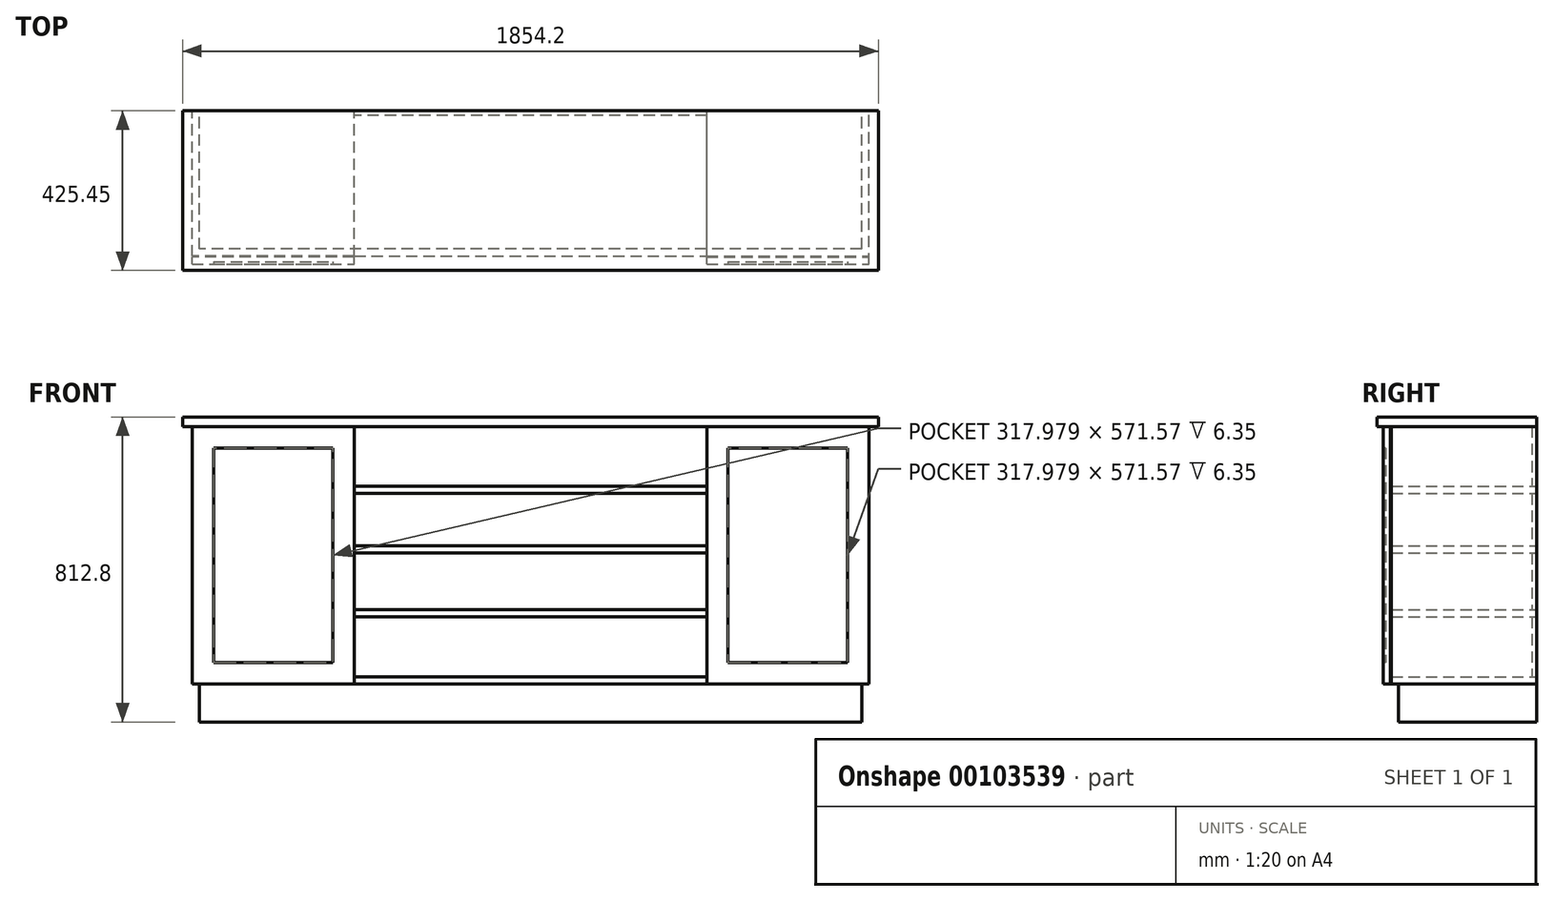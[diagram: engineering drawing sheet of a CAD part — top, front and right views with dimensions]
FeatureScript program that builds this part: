
annotation { "Feature Type Name" : "Feature", "Feature Type Description" : "" }
export const myFeature = defineFeature(function(context is Context, id is Id, definition is map)
    precondition{}
    {
        {
            var Q0;
            Q0=qCreatedBy(makeId("Front.planeOp"),FACE);
            var sketch = newSketch(context, id + "F0", { "sketchPlane" : qUnion([Q0])});
            skLineSegment(sketch, "E0.left", {"start": v(-901.7, 385.95) * mm, "end": v(-901.7, -299.85) * mm});
            skLineSegment(sketch, "E0.right", {"start": v(901.7, 385.95) * mm, "end": v(901.7, -299.85) * mm});
            skLineSegment(sketch, "E1", {"start": v(-901.7, 385.95) * mm, "end": v(-927.1, 385.95) * mm});
            skLineSegment(sketch, "E2", {"start": v(-927.1, 385.95) * mm, "end": v(-927.1, 411.35) * mm});
            skLineSegment(sketch, "E3", {"start": v(-927.1, 411.35) * mm, "end": v(927.1, 411.35) * mm});
            skLineSegment(sketch, "E4", {"start": v(927.1, 411.35) * mm, "end": v(927.1, 385.95) * mm});
            skLineSegment(sketch, "E5", {"start": v(901.7, 385.95) * mm, "end": v(927.1, 385.95) * mm});
            skLineSegment(sketch, "E6", {"start": v(-901.7, -299.85) * mm, "end": v(-882.65, -299.85) * mm});
            skLineSegment(sketch, "E7", {"start": v(-882.65, -299.85) * mm, "end": v(-882.65, -401.45) * mm});
            skLineSegment(sketch, "E8", {"start": v(-882.65, -401.45) * mm, "end": v(882.65, -401.45) * mm});
            skLineSegment(sketch, "E9", {"start": v(882.65, -401.45) * mm, "end": v(882.65, -299.85) * mm});
            skLineSegment(sketch, "E10", {"start": v(-469.5, 385.95) * mm, "end": v(-469.5, -299.85) * mm});
            skLineSegment(sketch, "E11", {"start": v(-901.7, 385.95) * mm, "end": v(-469.5, 385.95) * mm});
            skLineSegment(sketch, "E12", {"start": v(-469.5, -299.85) * mm, "end": v(-901.7, -299.85) * mm});
            skLineSegment(sketch, "E13", {"start": v(901.7, 385.95) * mm, "end": v(469.5, 385.95) * mm});
            skLineSegment(sketch, "E14", {"start": v(469.5, 385.95) * mm, "end": v(469.5, -299.85) * mm});
            skLineSegment(sketch, "E15", {"start": v(-469.5, -299.85) * mm, "end": v(469.5, -299.85) * mm});
            skLineSegment(sketch, "E16", {"start": v(469.5, -299.85) * mm, "end": v(901.7, -299.85) * mm});
            skLineSegment(sketch, "E17", {"start": v(469.5, 385.95) * mm, "end": v(-469.5, 385.95) * mm});
            skLineSegment(sketch, "E18.bottom", {"start": v(-844.59, 328.84) * mm, "end": v(-526.6, 328.84) * mm});
            skLineSegment(sketch, "E18.top", {"start": v(-844.59, -242.73) * mm, "end": v(-526.6, -242.73) * mm});
            skLineSegment(sketch, "E18.left", {"start": v(-844.59, 328.84) * mm, "end": v(-844.59, -242.73) * mm});
            skLineSegment(sketch, "E18.right", {"start": v(-526.6, 328.84) * mm, "end": v(-526.6, -242.73) * mm});
            skLineSegment(sketch, "E19.bottom", {"start": v(526.6, 328.84) * mm, "end": v(844.59, 328.84) * mm});
            skLineSegment(sketch, "E19.top", {"start": v(526.6, -242.73) * mm, "end": v(844.59, -242.73) * mm});
            skLineSegment(sketch, "E19.left", {"start": v(526.6, 328.84) * mm, "end": v(526.6, -242.73) * mm});
            skLineSegment(sketch, "E19.right", {"start": v(844.59, 328.84) * mm, "end": v(844.59, -242.73) * mm});
            skLineSegment(sketch, "E20", {"start": v(-526.6, 328.84) * mm, "end": v(-526.6, 385.95) * mm, "construction": true});
            skLineSegment(sketch, "E21", {"start": v(-526.6, 385.95) * mm, "end": v(-526.6, 328.84) * mm, "construction": true});
            skLineSegment(sketch, "E22", {"start": v(-526.6, 328.84) * mm, "end": v(-469.5, 328.84) * mm, "construction": true});
            skLineSegment(sketch, "E23", {"start": v(526.6, -242.73) * mm, "end": v(469.5, -242.73) * mm, "construction": true});
            skLineSegment(sketch, "E24", {"start": v(469.5, -242.73) * mm, "end": v(526.6, -242.73) * mm, "construction": true});
            skLineSegment(sketch, "E25", {"start": v(526.6, -242.73) * mm, "end": v(526.6, -299.85) * mm, "construction": true});
            skLineSegment(sketch, "E26", {"start": v(844.59, 328.84) * mm, "end": v(844.59, 385.95) * mm, "construction": true});
            skLineSegment(sketch, "E27", {"start": v(844.59, 385.95) * mm, "end": v(844.59, 328.84) * mm, "construction": true});
            skLineSegment(sketch, "E28", {"start": v(844.59, 328.84) * mm, "end": v(901.7, 328.84) * mm, "construction": true});
            skLineSegment(sketch, "E29", {"start": v(-844.59, -242.73) * mm, "end": v(-844.59, -299.85) * mm, "construction": true});
            skLineSegment(sketch, "E30", {"start": v(-469.5, -299.85) * mm, "end": v(-469.5, -280.8) * mm});
            skLineSegment(sketch, "E31", {"start": v(-469.5, -280.8) * mm, "end": v(469.5, -280.8) * mm});
            skLineSegment(sketch, "E32", {"start": v(469.5, -121.65) * mm, "end": v(-469.5, -121.65) * mm});
            skLineSegment(sketch, "E33", {"start": v(-469.5, -121.65) * mm, "end": v(-469.5, -102.6) * mm});
            skLineSegment(sketch, "E34", {"start": v(-469.5, -102.6) * mm, "end": v(469.5, -102.6) * mm});
            skLineSegment(sketch, "E35", {"start": v(469.5, 207.73) * mm, "end": v(-469.5, 207.73) * mm});
            skLineSegment(sketch, "E36", {"start": v(-469.5, 207.73) * mm, "end": v(-469.5, 226.78) * mm});
            skLineSegment(sketch, "E37", {"start": v(-469.5, 226.78) * mm, "end": v(469.5, 226.78) * mm});
            skLineSegment(sketch, "E38", {"start": v(-469.5, 67.6) * mm, "end": v(469.5, 67.6) * mm});
            skLineSegment(sketch, "E39", {"start": v(469.5, 48.56) * mm, "end": v(-469.5, 48.56) * mm});
            skPoint(sketch, "E40.endSnap0", {"position": v(0, 48.56) * mm});
            skPoint(sketch, "E41.endSnap0", {"position": v(0, 67.6) * mm});
            skLineSegment(sketch, "E42", {"start": v(-844.59, -242.73) * mm, "end": v(-901.7, -242.73) * mm, "construction": true});
            skLineSegment(sketch, "E43", {"start": v(299, 385.95) * mm, "end": v(299, 226.78) * mm, "construction": true});
            skLineSegment(sketch, "E44", {"start": v(299, 226.78) * mm, "end": v(299, 207.73) * mm, "construction": true});
            skLineSegment(sketch, "E45", {"start": v(299, 207.73) * mm, "end": v(299, 67.6) * mm, "construction": true});
            skLineSegment(sketch, "E46", {"start": v(299, 67.6) * mm, "end": v(299, 48.56) * mm, "construction": true});
            skLineSegment(sketch, "E47", {"start": v(299, 48.56) * mm, "end": v(299, -102.6) * mm, "construction": true});
            skLineSegment(sketch, "E48", {"start": v(299, -102.6) * mm, "end": v(299, -121.65) * mm, "construction": true});
            skLineSegment(sketch, "E49", {"start": v(299, -121.65) * mm, "end": v(299, -280.8) * mm, "construction": true});
            skLineSegment(sketch, "E50", {"start": v(299, -280.8) * mm, "end": v(299, -299.85) * mm, "construction": true});
            skSolve(sketch);
        }
        {
            var Q0;
            {var subQ5=sQuery(id+"F0.wireOp",EDGE,"E0.left");Q0=makeQuery(id+"F0.imprint","IMPRINT",FACE,{"disambiguationData":[TD([[makeQuery(id+"F0.imprint","IMPRINT",EDGE,{"derivedFrom":subQ5}),1.0]])]});}
            var Q1;
            {var subQ9=sQuery(id+"F0.wireOp",EDGE,"E0.right");Q1=makeQuery(id+"F0.imprint","IMPRINT",FACE,{"disambiguationData":[TD([[makeQuery(id+"F0.imprint","IMPRINT",EDGE,{"derivedFrom":subQ9}),-1.0]])]});}
            var Q2;
            Q2=makeQuery(id+"F0.imprint","IMPRINT",FACE,{"disambiguationData":[TD([[makeQuery(id+"F0.imprint","IMPRINT",EDGE,{"derivedFrom":sQuery(id+"F0.wireOp",EDGE,"E18.bottom")}),-1.0]])]});
            var Q3;
            Q3=makeQuery(id+"F0.imprint","IMPRINT",FACE,{"disambiguationData":[TD([[makeQuery(id+"F0.imprint","IMPRINT",EDGE,{"derivedFrom":sQuery(id+"F0.wireOp",EDGE,"E19.bottom")}),-1.0]])]});
            extrude(context, id + "F1", {"entities" : qUnion([Q0, Q1, Q2, Q3]), "depth" : 408.94 * mm});
        }
        {
            var Q0;
            {var subQ0=sQuery(id+"F0.wireOp",EDGE,"E35");Q0=makeQuery(id+"F0.imprint","IMPRINT",FACE,{"disambiguationData":[TD([[makeQuery(id+"F0.imprint","IMPRINT",EDGE,{"derivedFrom":subQ0}),-1.0]])]});}
            var Q1;
            {var subQ0=sQuery(id+"F0.wireOp",EDGE,"E38");Q1=makeQuery(id+"F0.imprint","IMPRINT",FACE,{"disambiguationData":[TD([[makeQuery(id+"F0.imprint","IMPRINT",EDGE,{"derivedFrom":subQ0}),-1.0]])]});}
            var Q2;
            {var subQ0=sQuery(id+"F0.wireOp",EDGE,"E32");Q2=makeQuery(id+"F0.imprint","IMPRINT",FACE,{"disambiguationData":[TD([[makeQuery(id+"F0.imprint","IMPRINT",EDGE,{"derivedFrom":subQ0}),-1.0]])]});}
            var Q3;
            {var subQ0=sQuery(id+"F0.wireOp",EDGE,"E15");Q3=makeQuery(id+"F0.imprint","IMPRINT",FACE,{"disambiguationData":[TD([[makeQuery(id+"F0.imprint","IMPRINT",EDGE,{"derivedFrom":subQ0}),1.0]])]});}
            extrude(context, id + "F2", {"entities" : qUnion([Q0, Q1, Q2, Q3]), "depth" : 387.35 * mm});
        }
        {
            var Q0;
            Q0=makeQuery(id+"F0.imprint","IMPRINT",FACE,{"disambiguationData":[TD([[makeQuery(id+"F0.imprint","IMPRINT",EDGE,{"derivedFrom":sQuery(id+"F0.wireOp",EDGE,"E1")}),-1.0]])]});
            extrude(context, id + "F3", {"entities" : qUnion([Q0]), "depth" : 425.45 * mm});
        }
        {
            var Q0;
            Q0=makeQuery(id+"F1.opExtrude","SWEPT_FACE",FACE,{"disambiguationData":[OSD([sQuery(id+"F0.wireOp",EDGE,"E0.left")])]});
            var sketch = newSketch(context, id + "F4", { "sketchPlane" : qUnion([Q0])});
            skLineSegment(sketch, "E51", {"start": v(408.94, 52.42) * mm, "end": v(389.9, 52.42) * mm, "construction": true});
            skLineSegment(sketch, "E52", {"start": v(389.9, -299.85) * mm, "end": v(389.9, 385.95) * mm});
            skLineSegment(sketch, "E53", {"start": v(389.9, 385.95) * mm, "end": v(387.35, 385.95) * mm});
            skLineSegment(sketch, "E54", {"start": v(387.35, 385.95) * mm, "end": v(387.35, -299.85) * mm});
            skLineSegment(sketch, "E55", {"start": v(387.35, -299.85) * mm, "end": v(389.9, -299.85) * mm});
            skLineSegment(sketch, "E56", {"start": v(389.9, 52.42) * mm, "end": v(387.35, 52.42) * mm, "construction": true});
            skPoint(sketch, "E56.endSnap0", {"position": v(387.35, 43.05) * mm});
            skSolve(sketch);
        }
        {
            var Q0;
            Q0=makeQuery(id+"F4.imprint","IMPRINT",FACE,{"disambiguationData":[TD([[makeQuery(id+"F4.imprint","IMPRINT",EDGE,{"derivedFrom":sQuery(id+"F4.wireOp",EDGE,"E52")}),1.0]])]});
            extrude(context, id + "F5", {"entities" : qUnion([Q0]), "operationType" : NewBodyOperationType.REMOVE, "endBound" : BoundingType.UP_TO_NEXT, "oppositeDirection" : true, "depth" : 25.4 * mm});
        }
        {
            var Q0;
            Q0=makeQuery(id+"F1.opExtrude","SWEPT_FACE",FACE,{"disambiguationData":[OSD([sQuery(id+"F0.wireOp",EDGE,"E0.right")])]});
            var sketch = newSketch(context, id + "F6", { "sketchPlane" : qUnion([Q0])});
            skLineSegment(sketch, "E57", {"start": v(-387.35, 385.95) * mm, "end": v(-387.35, -299.85) * mm});
            skPoint(sketch, "E58.endSnap0", {"position": v(-387.35, 43.05) * mm});
            skLineSegment(sketch, "E59.MirrorCS", {"start": v(-387.35, -299.85) * mm, "end": v(-389.9, -299.85) * mm});
            skLineSegment(sketch, "E60.MirrorCS", {"start": v(-389.9, 385.95) * mm, "end": v(-387.35, 385.95) * mm});
            skLineSegment(sketch, "E61.MirrorCS", {"start": v(-389.9, -299.85) * mm, "end": v(-389.9, 385.95) * mm});
            skLineSegment(sketch, "E62", {"start": v(-389.9, 43.05) * mm, "end": v(-408.94, 43.05) * mm, "construction": true});
            skSolve(sketch);
        }
        {
            var Q0;
            Q0=makeQuery(id+"F6.imprint","IMPRINT",FACE,{"disambiguationData":[TD([[makeQuery(id+"F6.imprint","IMPRINT",EDGE,{"derivedFrom":sQuery(id+"F6.wireOp",EDGE,"E57")}),-1.0]])]});
            extrude(context, id + "F7", {"entities" : qUnion([Q0]), "endBound" : BoundingType.UP_TO_NEXT, "oppositeDirection" : true, "depth" : 25.4 * mm});
        }
        {
            var Q0;
            {var subQ1=sQuery(id+"F0.wireOp",EDGE,"E7");Q0=makeQuery(id+"F0.imprint","IMPRINT",FACE,{"disambiguationData":[TD([[makeQuery(id+"F0.imprint","IMPRINT",EDGE,{"derivedFrom":subQ1}),1.0]])]});}
            extrude(context, id + "F8", {"entities" : qUnion([Q0]), "depth" : 368.3 * mm});
        }
        {
            var Q0;
            {var subQ0=sQuery(id+"F0.wireOp",EDGE,"E17");Q0=makeQuery(id+"F0.imprint","IMPRINT",FACE,{"disambiguationData":[TD([[makeQuery(id+"F0.imprint","IMPRINT",EDGE,{"derivedFrom":subQ0}),1.0]])]});}
            var Q1;
            {var subQ0=sQuery(id+"F0.wireOp",EDGE,"E35");Q1=makeQuery(id+"F0.imprint","IMPRINT",FACE,{"disambiguationData":[TD([[makeQuery(id+"F0.imprint","IMPRINT",EDGE,{"derivedFrom":subQ0}),1.0]])]});}
            var Q2;
            {var subQ0=sQuery(id+"F0.wireOp",EDGE,"E34");Q2=makeQuery(id+"F0.imprint","IMPRINT",FACE,{"disambiguationData":[TD([[makeQuery(id+"F0.imprint","IMPRINT",EDGE,{"derivedFrom":subQ0}),1.0]])]});}
            var Q3;
            {var subQ0=sQuery(id+"F0.wireOp",EDGE,"E31");Q3=makeQuery(id+"F0.imprint","IMPRINT",FACE,{"disambiguationData":[TD([[makeQuery(id+"F0.imprint","IMPRINT",EDGE,{"derivedFrom":subQ0}),1.0]])]});}
            extrude(context, id + "F9", {"entities" : qUnion([Q0, Q1, Q2, Q3]), "depth" : 12.7 * mm});
        }
        {
            var Q0;
            Q0=makeQuery(id+"F1.opExtrude","CAP_FACE",FACE,{"disambiguationData":[OSD([sQuery(id+"F0.wireOp",EDGE,"E0.left"),sQuery(id+"F0.wireOp",EDGE,"E10"),sQuery(id+"F0.wireOp",EDGE,"E11"),sQuery(id+"F0.wireOp",EDGE,"E12"),sQuery(id+"F0.wireOp",EDGE,"E30"),sQuery(id+"F0.wireOp",EDGE,"E33"),sQuery(id+"F0.wireOp",EDGE,"E36")])],"isStart":false});
            var sketch = newSketch(context, id + "F10", { "sketchPlane" : qUnion([Q0])});
            skLineSegment(sketch, "E63.0", {"start": v(-844.59, 328.84) * mm, "end": v(-526.6, 328.84) * mm});
            skLineSegment(sketch, "E64.0", {"start": v(-526.6, 328.84) * mm, "end": v(-526.6, -242.73) * mm});
            skLineSegment(sketch, "E65.0", {"start": v(-844.59, -242.73) * mm, "end": v(-526.6, -242.73) * mm});
            skLineSegment(sketch, "E66.0", {"start": v(-844.59, 328.84) * mm, "end": v(-844.59, -242.73) * mm});
            skLineSegment(sketch, "E67.0", {"start": v(526.6, 328.84) * mm, "end": v(526.6, -242.73) * mm});
            skLineSegment(sketch, "E68.0", {"start": v(526.6, 328.84) * mm, "end": v(844.59, 328.84) * mm});
            skLineSegment(sketch, "E69.0", {"start": v(844.59, 328.84) * mm, "end": v(844.59, -242.73) * mm});
            skLineSegment(sketch, "E70.0", {"start": v(526.6, -242.73) * mm, "end": v(844.59, -242.73) * mm});
            skSolve(sketch);
        }
        {
            var Q0;
            Q0=makeQuery(id+"F10.imprint","IMPRINT",FACE,{"disambiguationData":[TD([[makeQuery(id+"F10.imprint","IMPRINT",EDGE,{"derivedFrom":sQuery(id+"F10.wireOp",EDGE,"E67.0")}),1.0]])]});
            var Q1;
            Q1=makeQuery(id+"F10.imprint","IMPRINT",FACE,{"disambiguationData":[TD([[makeQuery(id+"F10.imprint","IMPRINT",EDGE,{"derivedFrom":sQuery(id+"F10.wireOp",EDGE,"E63.0")}),-1.0]])]});
            extrude(context, id + "F11", {"entities" : qUnion([Q0, Q1]), "operationType" : NewBodyOperationType.REMOVE, "oppositeDirection" : true, "depth" : 6.35 * mm});
        }
    });
